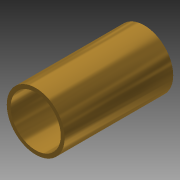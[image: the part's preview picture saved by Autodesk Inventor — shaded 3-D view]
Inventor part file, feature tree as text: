
AUTODESK INVENTOR PART (.ipt)
format: ipt  version: 2014 (Build 180170000, 170)  size: 85,504 bytes
history: native  units: in
note: dims shown in document units (in); Inventor stores cm internally (conversion verified against a paired STEP export)
features: extrude x1, sketch x1
ambient origin geometry x8: Origin, YZ Plane, XZ Plane, XY Plane, X Axis, Y Axis, Z Axis, Center Point
bodies: Solid1 (feature_tree)
feature tree (2):
  extrude  "Extrusion1"  Depth=0.82in
  sketch  "Sketch1"  dims[d0=0.379in d2=0.437in d3=0.82in d4=0.0in]
